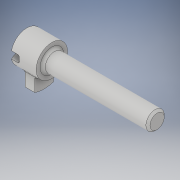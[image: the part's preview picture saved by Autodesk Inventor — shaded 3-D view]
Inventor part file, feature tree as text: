
AUTODESK INVENTOR PART (.ipt)
format: ipt  version: 2018.3 (Build 223284000, 284)  size: 175,616 bytes
history: native  units: in
note: dims shown in document units (in); Inventor stores cm internally (conversion verified against a paired STEP export)
features: sketch x3, extrude x2, revolve x1, plane x1, fillet x1
ambient origin geometry x8: Origin, YZ Plane, XZ Plane, XY Plane, X Axis, Y Axis, Z Axis, Center Point
bodies: Solid1 (feature_tree)
feature tree (8):
  revolve  "Revolution1"  [1 undecoded]
  extrude  "Extrusion1"  Depth=0.045in
  plane  "Work Plane1"
  extrude  "Extrusion2"  Depth=0.01in
  fillet  "Fillet1"  Radius=0.013in
  sketch  "Sketch1"  dims[d0=0.66in d1=0.077in]
  sketch  "Sketch2"  dims[d2=0.517in d3=0.045in]
  sketch  "Sketch4"  dims[d4=0.01in d5=0.01in d6=0.013in d8=0.32in d9=90.0deg d10=0.0175in d11=0.06in d12=0.01in d13=1.0in d14=0.0in d18=-0.038in d19=0.0455in d20=0.0455in d21=0.047in d22=0.0in d23=0.01in]
note: 1 required parameter value undecoded (feature->parameter linkage not recoverable at this tier; creation-order binding heuristic only, values carry confidence <= 0.55)
